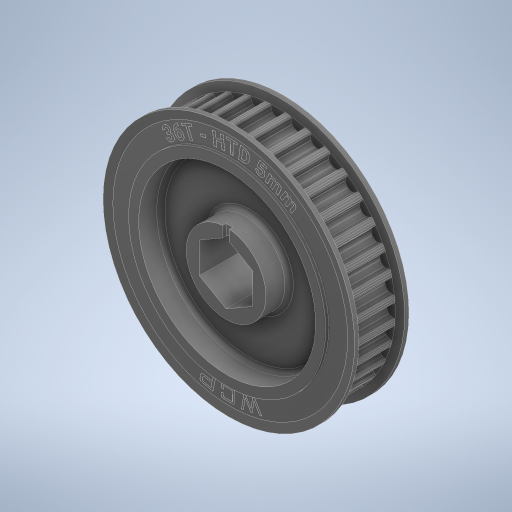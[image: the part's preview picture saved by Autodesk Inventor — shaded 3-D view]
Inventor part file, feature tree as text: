
AUTODESK INVENTOR PART (.ipt)
format: ipt  version: 2024 (Build 280153000, 153)  size: 1,208,832 bytes
history: native  units: in
note: dims shown in document units (in); Inventor stores cm internally (conversion verified against a paired STEP export)
features: mirror x2, other x1
ambient origin geometry x8: Origin, YZ Plane, XZ Plane, XY Plane, X Axis, Y Axis, Z Axis, Center Point
bodies: Solid1 (feature_tree), Solid2 (feature_tree), Solid3 (feature_tree)
feature tree (3):
  mirror  "Mirror1"
  mirror  "Mirror1:1"
  other  "Cut-Extrude5"
